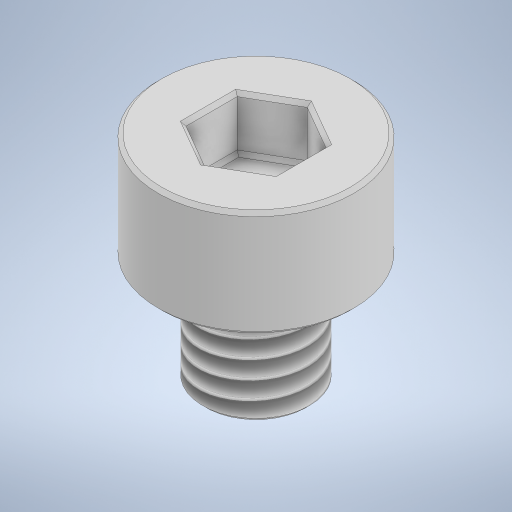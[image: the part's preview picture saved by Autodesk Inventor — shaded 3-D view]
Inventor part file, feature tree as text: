
AUTODESK INVENTOR PART (.ipt)
format: ipt  version: 2023 (Build 270158000, 158)  size: 289,280 bytes
history: native  units: in
note: dims shown in document units (in); Inventor stores cm internally (conversion verified against a paired STEP export)
features: sketch x2, revolve x1, thread x1, extrude x1, chamfer x1
ambient origin geometry x8: Origin, YZ Plane, XZ Plane, XY Plane, X Axis, Y Axis, Z Axis, Center Point
bodies: Solid1 (feature_tree)
feature tree (6):
  revolve  "Revolution1"  [1 undecoded]
  thread  "Thread1"  [1 undecoded]
  extrude  "Extrusion2"  TaperAngle=90.0deg  [1 undecoded]
  chamfer  "Chamfer2"  Distance=0.1181in
  sketch  "Sketch1"  dims[d0=0.1083in d1=0.1181in d2=0.1181in]
  sketch  "Sketch3"  dims[d3=0.0591in d4=90.0deg d5=0.1181in d6=0.0in d13=0.0984in d14=0.0591in d15=0.0in d16=0.0039in d17=0.0787in d18=45.0deg]
note: 3 required parameter values undecoded (feature->parameter linkage not recoverable at this tier; creation-order binding heuristic only, values carry confidence <= 0.55)